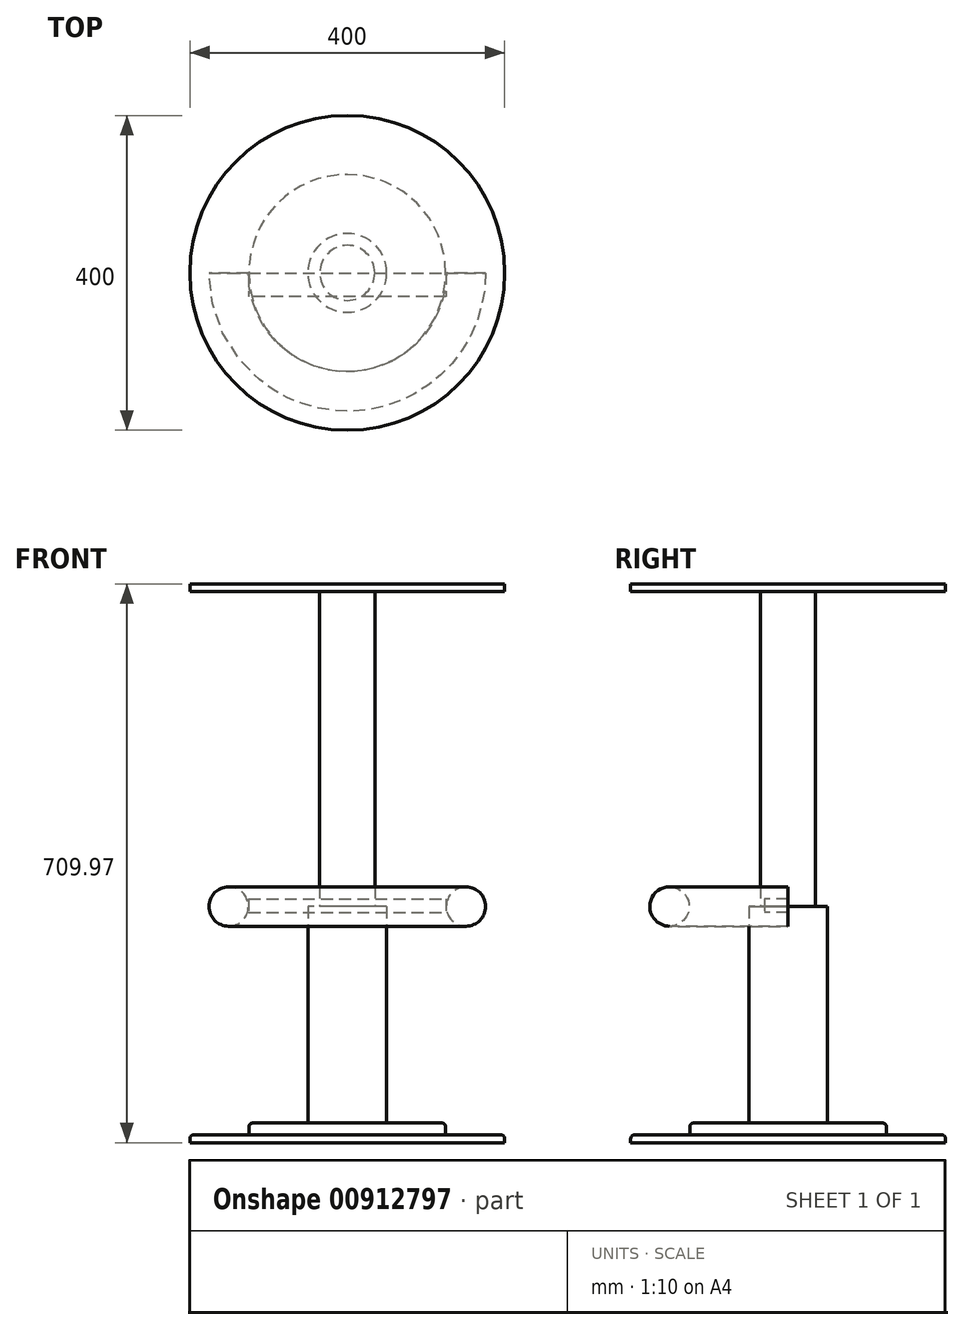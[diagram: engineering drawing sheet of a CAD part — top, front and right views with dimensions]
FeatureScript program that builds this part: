
annotation { "Feature Type Name" : "Feature", "Feature Type Description" : "" }
export const myFeature = defineFeature(function(context is Context, id is Id, definition is map)
    precondition{}
    {
        {
            var Q0;
            Q0=qCreatedBy(makeId("Top.planeOp"),FACE);
            cPlane(context, id + "F0", {"entities" : qUnion([Q0]), "cplaneType" : CPlaneType.OFFSET, "offset" : 299.97 * mm, "oppositeDirection" : true, "width" : 152.4 * mm, "height" : 152.4 * mm});
        }
        {
            var Q0;
            Q0=qCreatedBy(id+"F0.planeOp",FACE);
            var sketch = newSketch(context, id + "F1", { "sketchPlane" : qUnion([Q0])});
            skCircle(sketch, "E0", {"center": v(0, 0) * mm, "radius": 200 * mm});
            skSolve(sketch);
        }
        {
            var Q0;
            Q0 = qSketchRegion(id + "F1", true);
            extrude(context, id + "F2", {"entities" : qUnion([Q0]), "depth" : 10 * mm, "offsetDistance" : 25.4 * mm});
        }
        {
            var Q0;
            Q0=makeQuery(id+"F2.opExtrude","CAP_FACE",FACE,{"disambiguationData":[OSD([sQuery(id+"F1.wireOp",EDGE,"E0")])],"isStart":false});
            var sketch = newSketch(context, id + "F3", { "sketchPlane" : qUnion([Q0])});
            skCircle(sketch, "E1", {"center": v(0, 0) * mm, "radius": 125 * mm});
            skSolve(sketch);
        }
        {
            var Q0;
            Q0 = qSketchRegion(id + "F3", true);
            extrude(context, id + "F4", {"entities" : qUnion([Q0]), "operationType" : NewBodyOperationType.ADD, "depth" : 15 * mm, "offsetDistance" : 25.4 * mm});
        }
        {
            var Q0;
            Q0=makeQuery(id+"F2.opExtrude","CAP_EDGE",EDGE,{"disambiguationData":[OSD([sQuery(id+"F1.wireOp",EDGE,"E0")])],"isStart":false});
            var Q1;
            Q1=makeQuery(id+"F4.opExtrude","CAP_EDGE",EDGE,{"disambiguationData":[OSD([sQuery(id+"F3.wireOp",EDGE,"E1")])],"isStart":false});
            fillet(context, id + "F5", {"entities" : qUnion([Q0, Q1]), "radius" : 5.08 * mm, "tangentPropagation" : true, "allowEdgeOverflow" : false});
        }
        {
            var Q0;
            Q0=makeQuery(id+"F4.opExtrude","CAP_FACE",FACE,{"disambiguationData":[OSD([sQuery(id+"F3.wireOp",EDGE,"E1")])],"isStart":false});
            var sketch = newSketch(context, id + "F6", { "sketchPlane" : qUnion([Q0])});
            skCircle(sketch, "E2", {"center": v(0, 0) * mm, "radius": 50 * mm});
            skSolve(sketch);
        }
        {
            var Q0;
            Q0 = qSketchRegion(id + "F6", true);
            extrude(context, id + "F7", {"entities" : qUnion([Q0]), "operationType" : NewBodyOperationType.ADD, "depth" : 275 * mm, "offsetDistance" : 25.4 * mm});
        }
        {
            var Q0;
            Q0=qCreatedBy(makeId("Top.planeOp"),FACE);
            var sketch = newSketch(context, id + "F8", { "sketchPlane" : qUnion([Q0])});
            skLineSegment(sketch, "E3", {"start": v(-49.8, 0) * mm, "end": v(-125.3, 0) * mm});
            skLineSegment(sketch, "E4", {"start": v(50, 0) * mm, "end": v(125.26, 0) * mm});
            skLineSegment(sketch, "E5", {"start": v(-125.3, 0) * mm, "end": v(-175.3, 0) * mm});
            skLineSegment(sketch, "E6", {"start": v(125.26, 0) * mm, "end": v(175.26, 0) * mm});
            skLineSegment(sketch, "E7", {"start": v(-125.3, 0) * mm, "end": v(-125.3, -30) * mm});
            skLineSegment(sketch, "E8", {"start": v(-125.3, 0) * mm, "end": v(125.26, 0) * mm});
            skLineSegment(sketch, "E9", {"start": v(125.26, 0) * mm, "end": v(125.26, -30) * mm});
            skLineSegment(sketch, "E10", {"start": v(125.26, -30) * mm, "end": v(-125.3, -30) * mm});
            skSolve(sketch);
        }
        {
            var Q0;
            Q0=qCreatedBy(makeId("Front.planeOp"),FACE);
            var sketch = newSketch(context, id + "F9", { "sketchPlane" : qUnion([Q0])});
            skCircle(sketch, "E11", {"center": v(-150.71, 0) * mm, "radius": 25 * mm});
            skSolve(sketch);
        }
        {
            var Q0;
            Q0 = qSketchRegion(id + "F9", true);
            var Q1;
            Q1=makeQuery(id+"F7.opExtrude","SWEPT_FACE",FACE,{"disambiguationData":[OSD([sQuery(id+"F6.wireOp",EDGE,"E2")])]});
            revolve(context, id + "F10", {"surfaceOperationType" : NewSurfaceOperationType.NEW, "entities" : qUnion([Q0]), "axis" : qUnion([Q1]), "revolveType" : RevolveType.ONE_DIRECTION, "oppositeDirection" : true, "angle" : 180 * degree});
        }
        {
            var Q0;
            {var subQ0=sQuery(id+"F8.wireOp",EDGE,"E7");Q0=makeQuery(id+"F8.imprint","IMPRINT",FACE,{"disambiguationData":[TD([[makeQuery(id+"F8.imprint","IMPRINT",EDGE,{"derivedFrom":subQ0}),1.0]])]});}
            extrude(context, id + "F11", {"entities" : qUnion([Q0]), "depth" : 17 * mm, "offsetDistance" : 25.4 * mm});
        }
        {
            var Q0;
            Q0=makeQuery(id+"F11.opExtrude","SWEPT_BODY",BODY,{"disambiguationData":[OSD([sQuery(id+"F8.wireOp",EDGE,"E7")])]});
            transform(context, id + "F12", {"entities" : qUnion([Q0]), "transformType" : TransformType.TRANSLATION_3D, "dx" : 0 * mm, "dy" : 0 * mm, "dz" : -7.5 * mm, "makeCopy" : false});
        }
        {
            var Q0;
            Q0=qCreatedBy(makeId("Top.planeOp"),FACE);
            var sketch = newSketch(context, id + "F13", { "sketchPlane" : qUnion([Q0])});
            skCircle(sketch, "E12", {"center": v(0, 0) * mm, "radius": 35 * mm});
            skSolve(sketch);
        }
        {
            var Q0;
            Q0 = qSketchRegion(id + "F13", true);
            extrude(context, id + "F14", {"entities" : qUnion([Q0]), "depth" : 400 * mm, "offsetDistance" : 25.4 * mm});
        }
        {
            var Q0;
            Q0=makeQuery(id+"F14.opExtrude","CAP_FACE",FACE,{"disambiguationData":[OSD([sQuery(id+"F13.wireOp",EDGE,"E12")])],"isStart":false});
            var sketch = newSketch(context, id + "F15", { "sketchPlane" : qUnion([Q0])});
            skCircle(sketch, "E13", {"center": v(0, 0) * mm, "radius": 200 * mm});
            skSolve(sketch);
        }
        {
            var Q0;
            Q0 = qSketchRegion(id + "F15", true);
            extrude(context, id + "F16", {"entities" : qUnion([Q0]), "operationType" : NewBodyOperationType.ADD, "depth" : 10 * mm, "offsetDistance" : 25.4 * mm});
        }
    });
